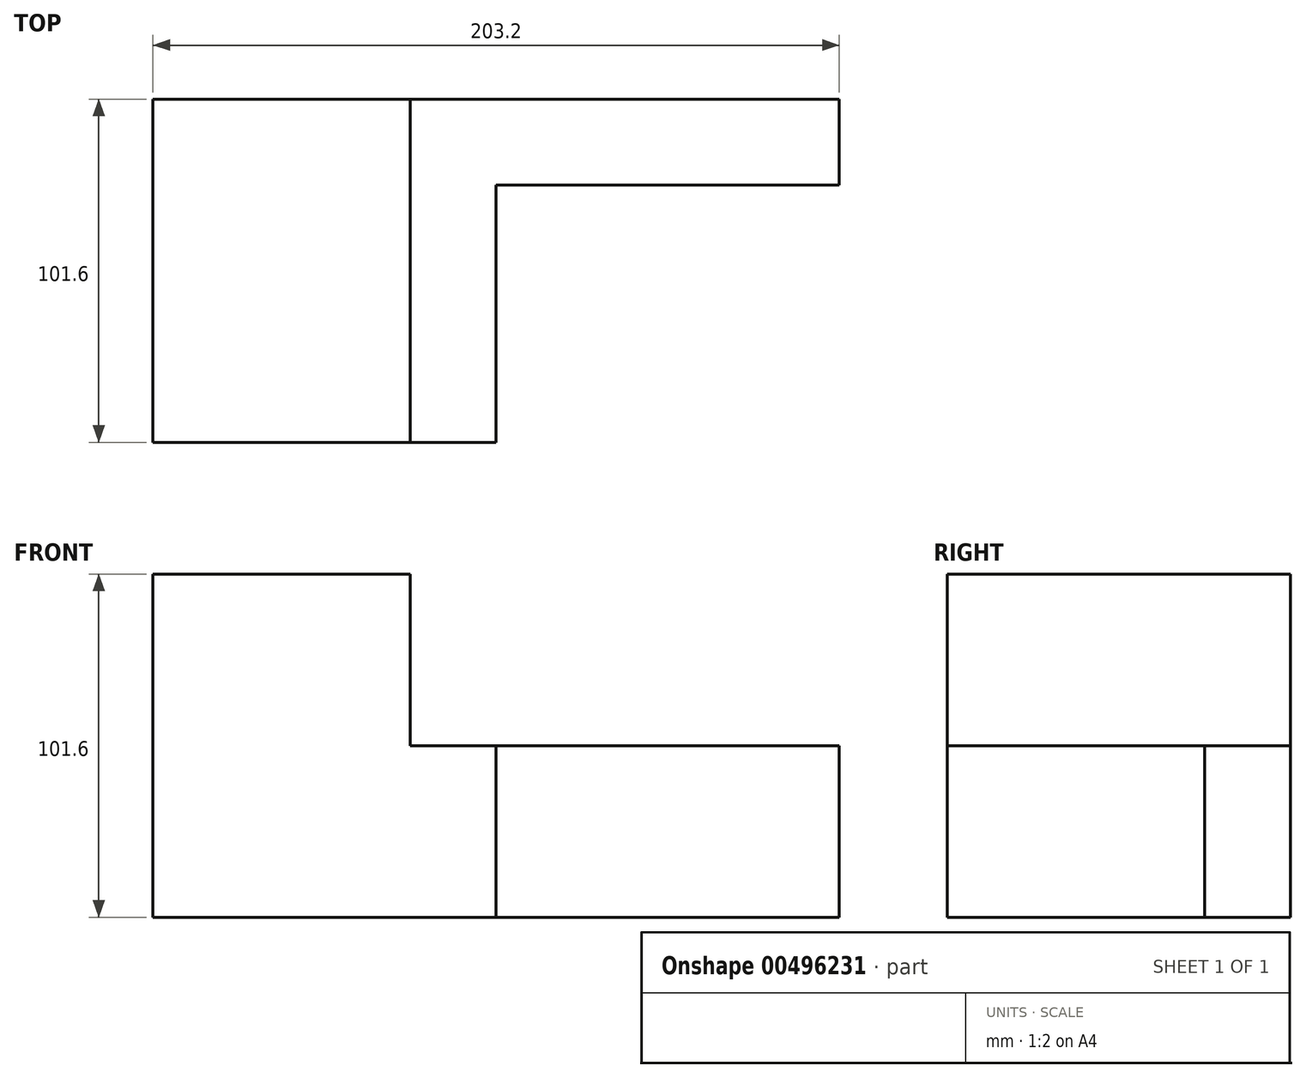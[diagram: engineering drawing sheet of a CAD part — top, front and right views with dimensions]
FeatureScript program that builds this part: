
annotation { "Feature Type Name" : "Feature", "Feature Type Description" : "" }
export const myFeature = defineFeature(function(context is Context, id is Id, definition is map)
    precondition{}
    {
        {
            var Q0;
            Q0=qCreatedBy(makeId("Front.planeOp"),FACE);
            var sketch = newSketch(context, id + "F0", { "sketchPlane" : qUnion([Q0])});
            skLineSegment(sketch, "E0.bottom", {"start": v(0, 0) * mm, "end": v(203.2, 0) * mm});
            skLineSegment(sketch, "E0.top", {"start": v(0, 101.6) * mm, "end": v(203.2, 101.6) * mm});
            skLineSegment(sketch, "E0.left", {"start": v(0, 0) * mm, "end": v(0, 101.6) * mm});
            skLineSegment(sketch, "E0.right", {"start": v(203.2, 0) * mm, "end": v(203.2, 101.6) * mm});
            skLineSegment(sketch, "E1.bottom", {"start": v(203.2, 101.6) * mm, "end": v(76.2, 101.6) * mm});
            skLineSegment(sketch, "E1.top", {"start": v(203.2, 50.8) * mm, "end": v(76.2, 50.8) * mm});
            skLineSegment(sketch, "E1.left", {"start": v(203.2, 101.6) * mm, "end": v(203.2, 50.8) * mm});
            skLineSegment(sketch, "E1.right", {"start": v(76.2, 101.6) * mm, "end": v(76.2, 50.8) * mm});
            skSolve(sketch);
        }
        {
            var Q0;
            Q0=makeQuery(id+"F0.imprint","IMPRINT",FACE,{"disambiguationData":[TD([[makeQuery(id+"F0.imprint","IMPRINT",EDGE,{"derivedFrom":sQuery(id+"F0.wireOp",EDGE,"E0.bottom")}),1.0]])]});
            extrude(context, id + "F1", {"entities" : qUnion([Q0]), "depth" : 101.6 * mm});
        }
        {
            var Q0;
            Q0=makeQuery(id+"F1.opExtrude","SWEPT_FACE",FACE,{"disambiguationData":[OSD([sQuery(id+"F0.wireOp",EDGE,"E1.top")])]});
            var sketch = newSketch(context, id + "F2", { "sketchPlane" : qUnion([Q0])});
            skLineSegment(sketch, "E2.bottom", {"start": v(203.2, -101.6) * mm, "end": v(101.6, -101.6) * mm});
            skLineSegment(sketch, "E2.top", {"start": v(203.2, -25.4) * mm, "end": v(101.6, -25.4) * mm});
            skLineSegment(sketch, "E2.left", {"start": v(203.2, -101.6) * mm, "end": v(203.2, -25.4) * mm});
            skLineSegment(sketch, "E2.right", {"start": v(101.6, -101.6) * mm, "end": v(101.6, -25.4) * mm});
            skSolve(sketch);
        }
        {
            var Q0;
            Q0 = qSketchRegion(id + "F2", true);
            extrude(context, id + "F3", {"entities" : qUnion([Q0]), "operationType" : NewBodyOperationType.REMOVE, "endBound" : BoundingType.UP_TO_NEXT, "oppositeDirection" : true, "depth" : 25.4 * mm});
        }
    });
